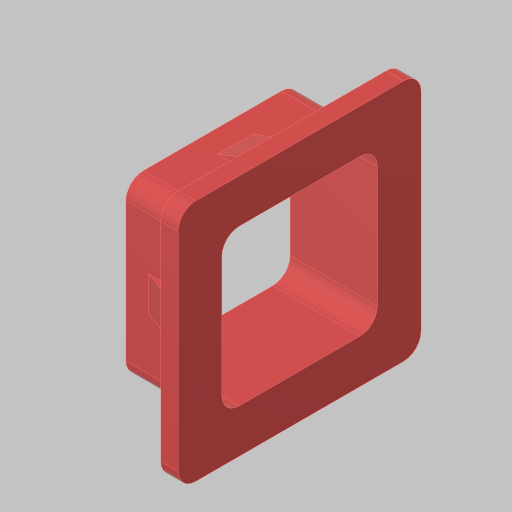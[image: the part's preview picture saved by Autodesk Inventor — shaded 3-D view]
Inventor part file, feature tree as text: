
AUTODESK INVENTOR PART (.ipt)
format: ipt  version: 2023.5 (Build 275446000, 446)  size: 164,352 bytes
history: native  units: in
note: dims shown in document units (in); Inventor stores cm internally (conversion verified against a paired STEP export)
features: extrude x3, sketch x3, fillet x1, pattern_circular x1, projected_geometry x1
ambient origin geometry x8: Origin, YZ Plane, XZ Plane, XY Plane, X Axis, Y Axis, Z Axis, Center Point
bodies: Solid1 (feature_tree)
feature tree (9):
  extrude  "Extrusion1"  Depth=1.24in
  extrude  "Extrusion2"  Depth=0.5in TaperAngle=0.0deg
  fillet  "Fillet1"  Radius=0.25in
  extrude  "Extrusion3"  Depth=0.125in
  pattern_circular  "Circular Pattern1"  [2 undecoded]
  sketch  "Sketch1"  dims[d0=1.24in d1=1.24in]
  sketch  "Sketch2"  dims[d2=0.0625in d3=0.5in d4=0.0in d5=0.25in]
  projected_geometry  "Projected Loop1"
  sketch  "Sketch4"  dims[d6=0.125in d7=0.0in d8=0.125in d9=0.13in d10=0.075in d11=0.1374in d12=0.25in d13=0.0in d14=1.5748in d15=360.0deg]
note: 2 required parameter values undecoded (feature->parameter linkage not recoverable at this tier; creation-order binding heuristic only, values carry confidence <= 0.55)
